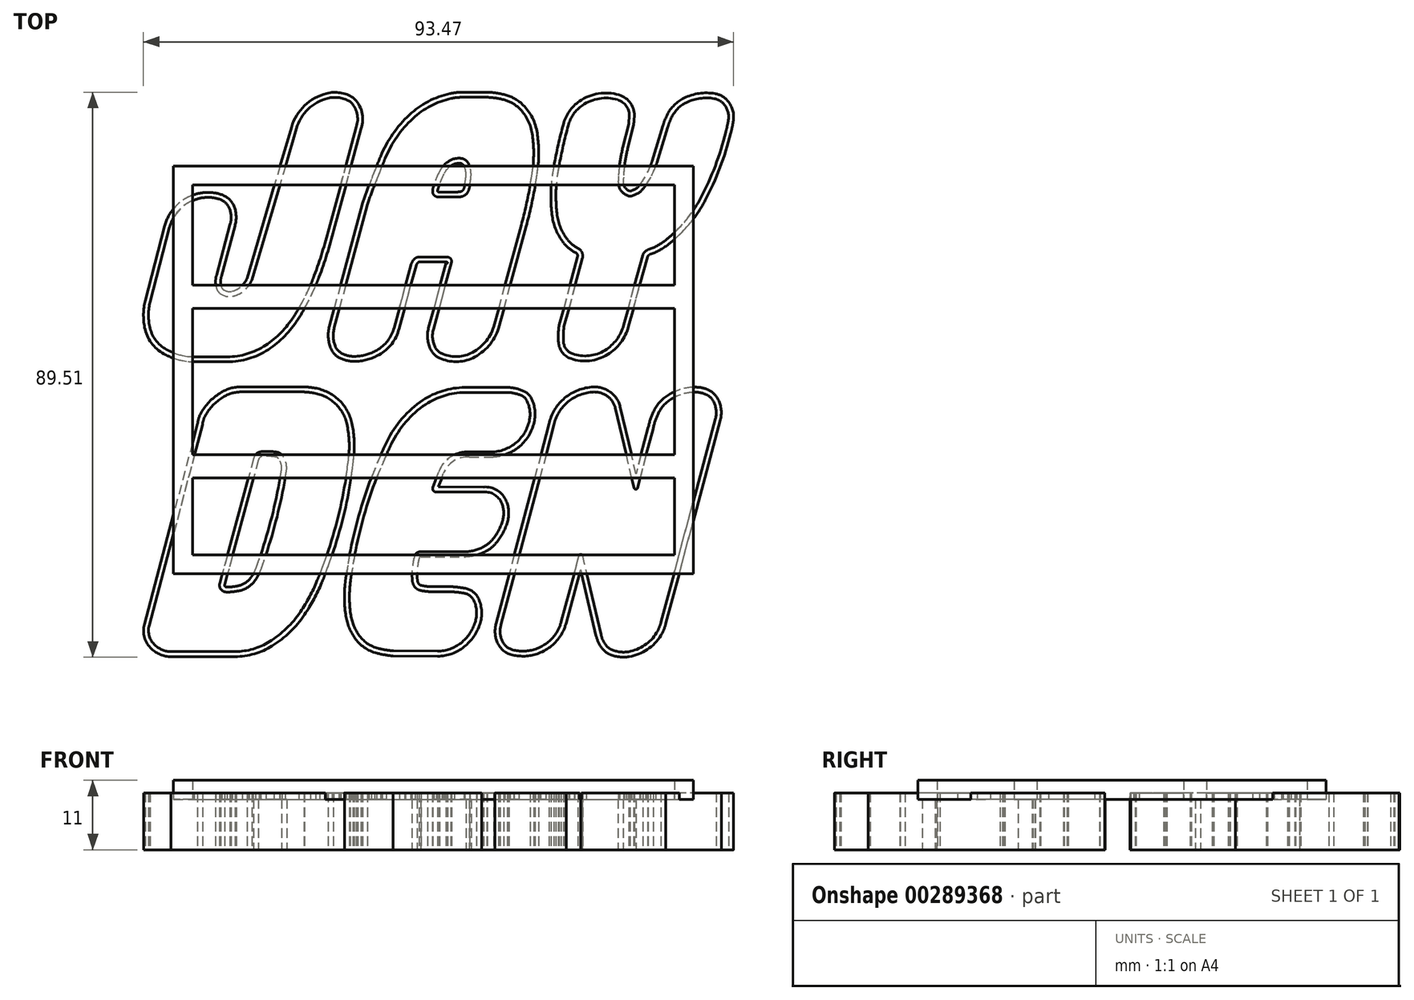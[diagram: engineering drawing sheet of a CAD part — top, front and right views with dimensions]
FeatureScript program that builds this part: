
annotation { "Feature Type Name" : "Feature", "Feature Type Description" : "" }
export const myFeature = defineFeature(function(context is Context, id is Id, definition is map)
    precondition{}
    {
        {
            var Q0;
            Q0=qCreatedBy(makeId("Top.planeOp"),FACE);
            var sketch = newSketch(context, id + "F0", { "sketchPlane" : qUnion([Q0])});
            skLineSegment(sketch, "E0", {"start": v(-12.96, 39.12) * mm, "end": v(-17.26, 23) * mm});
            skArc(sketch, "E1", {"start": v(-17.26, 23) * mm, "mid": v(-18.34, 19.28) * mm, "end": v(-19.6, 15.63) * mm});
            skArc(sketch, "E2", {"start": v(-19.6, 15.63) * mm, "mid": v(-21.14, 12.1) * mm, "end": v(-23.08, 8.76) * mm});
            skArc(sketch, "E3", {"start": v(-23.08, 8.76) * mm, "mid": v(-25.13, 6.3) * mm, "end": v(-27.66, 4.35) * mm});
            skArc(sketch, "E4", {"start": v(-27.66, 4.35) * mm, "mid": v(-30.6, 3.1) * mm, "end": v(-33.77, 2.75) * mm});
            skLineSegment(sketch, "E5", {"start": v(-33.77, 2.75) * mm, "end": v(-38.52, 2.75) * mm});
            skArc(sketch, "E6", {"start": v(-38.52, 2.75) * mm, "mid": v(-40.84, 3.04) * mm, "end": v(-43.02, 3.9) * mm});
            skArc(sketch, "E7", {"start": v(-43.02, 3.9) * mm, "mid": v(-44.75, 5.43) * mm, "end": v(-45.68, 7.55) * mm});
            skArc(sketch, "E8", {"start": v(-45.68, 7.55) * mm, "mid": v(-45.85, 9.5) * mm, "end": v(-45.6, 11.44) * mm});
            skLineSegment(sketch, "E9", {"start": v(-45.6, 11.44) * mm, "end": v(-42.52, 23.25) * mm});
            skArc(sketch, "E10", {"start": v(-42.52, 23.25) * mm, "mid": v(-40.4, 26.55) * mm, "end": v(-36.76, 27.98) * mm});
            skArc(sketch, "E11", {"start": v(-36.76, 27.98) * mm, "mid": v(-35.62, 27.94) * mm, "end": v(-34.51, 27.67) * mm});
            skArc(sketch, "E12", {"start": v(-34.51, 27.67) * mm, "mid": v(-33.6, 27.1) * mm, "end": v(-33.02, 26.22) * mm});
            skArc(sketch, "E13", {"start": v(-33.02, 26.22) * mm, "mid": v(-32.77, 24.97) * mm, "end": v(-32.93, 23.7) * mm});
            skLineSegment(sketch, "E14", {"start": v(-32.93, 23.7) * mm, "end": v(-35.1, 15.7) * mm});
            skArc(sketch, "E15", {"start": v(-35.1, 15.7) * mm, "mid": v(-35.23, 14.66) * mm, "end": v(-35.1, 13.63) * mm});
            skArc(sketch, "E16", {"start": v(-35.1, 13.63) * mm, "mid": v(-34.93, 13.22) * mm, "end": v(-34.64, 12.89) * mm});
            skArc(sketch, "E17", {"start": v(-34.64, 12.89) * mm, "mid": v(-33.6, 12.35) * mm, "end": v(-32.42, 12.35) * mm});
            skArc(sketch, "E18", {"start": v(-32.42, 12.35) * mm, "mid": v(-30.64, 13.29) * mm, "end": v(-29.5, 14.94) * mm});
            skLineSegment(sketch, "E19", {"start": v(-29.5, 14.94) * mm, "end": v(-22.42, 38.92) * mm});
            skArc(sketch, "E20", {"start": v(-22.42, 38.92) * mm, "mid": v(-20.57, 41.97) * mm, "end": v(-17.45, 43.7) * mm});
            skArc(sketch, "E21", {"start": v(-17.45, 43.7) * mm, "mid": v(-15.64, 43.79) * mm, "end": v(-13.94, 43.18) * mm});
            skArc(sketch, "E22", {"start": v(-13.94, 43.18) * mm, "mid": v(-12.83, 41.3) * mm, "end": v(-12.96, 39.12) * mm});
            skLineSegment(sketch, "E23", {"start": v(8.82, 7.5) * mm, "end": v(13.19, 23.62) * mm});
            skArc(sketch, "E24", {"start": v(13.19, 23.62) * mm, "mid": v(14.17, 27.72) * mm, "end": v(14.91, 31.87) * mm});
            skArc(sketch, "E25", {"start": v(14.91, 31.87) * mm, "mid": v(15.15, 34.97) * mm, "end": v(14.92, 38.07) * mm});
            skArc(sketch, "E26", {"start": v(14.92, 38.07) * mm, "mid": v(14.24, 40.23) * mm, "end": v(12.92, 42.06) * mm});
            skArc(sketch, "E27", {"start": v(12.92, 42.06) * mm, "mid": v(11.83, 42.9) * mm, "end": v(10.57, 43.43) * mm});
            skArc(sketch, "E28", {"start": v(10.57, 43.43) * mm, "mid": v(9.18, 43.73) * mm, "end": v(7.76, 43.86) * mm});
            skLineSegment(sketch, "E29", {"start": v(7.76, 43.86) * mm, "end": v(3.8, 43.85) * mm});
            skArc(sketch, "E30", {"start": v(3.8, 43.85) * mm, "mid": v(2.94, 43.8) * mm, "end": v(2.1, 43.67) * mm});
            skArc(sketch, "E31", {"start": v(2.1, 43.67) * mm, "mid": v(-1.17, 42.49) * mm, "end": v(-4, 40.48) * mm});
            skArc(sketch, "E32", {"start": v(-4, 40.48) * mm, "mid": v(-6.51, 37.57) * mm, "end": v(-8.36, 34.2) * mm});
            skArc(sketch, "E33", {"start": v(-8.36, 34.2) * mm, "mid": v(-9.82, 30.55) * mm, "end": v(-11.2, 26.86) * mm});
            skLineSegment(sketch, "E34", {"start": v(-11.2, 26.86) * mm, "end": v(-16.43, 7.36) * mm});
            skArc(sketch, "E35", {"start": v(-16.43, 7.36) * mm, "mid": v(-16.58, 5.89) * mm, "end": v(-16.28, 4.44) * mm});
            skArc(sketch, "E36", {"start": v(-16.28, 4.44) * mm, "mid": v(-15.88, 3.79) * mm, "end": v(-15.28, 3.32) * mm});
            skArc(sketch, "E37", {"start": v(-15.28, 3.32) * mm, "mid": v(-14.19, 2.9) * mm, "end": v(-13.02, 2.81) * mm});
            skArc(sketch, "E38", {"start": v(-13.02, 2.81) * mm, "mid": v(-11.32, 3.1) * mm, "end": v(-9.73, 3.77) * mm});
            skArc(sketch, "E39", {"start": v(-9.73, 3.77) * mm, "mid": v(-7.97, 5.28) * mm, "end": v(-6.94, 7.36) * mm});
            skLineSegment(sketch, "E40", {"start": v(-6.94, 7.36) * mm, "end": v(-4.23, 17.4) * mm});
            skArc(sketch, "E41", {"start": v(-4.23, 17.4) * mm, "mid": v(-4.04, 17.85) * mm, "end": v(-3.74, 18.24) * mm});
            skArc(sketch, "E42", {"start": v(-3.74, 18.24) * mm, "mid": v(-3.4, 18.47) * mm, "end": v(-3.02, 18.56) * mm});
            skLineSegment(sketch, "E43", {"start": v(-3.02, 18.56) * mm, "end": v(1.38, 18.55) * mm});
            skArc(sketch, "E44", {"start": v(1.38, 18.55) * mm, "mid": v(1.6, 18.53) * mm, "end": v(1.8, 18.45) * mm});
            skArc(sketch, "E45", {"start": v(1.8, 18.45) * mm, "mid": v(2.08, 18.17) * mm, "end": v(2.14, 17.79) * mm});
            skLineSegment(sketch, "E46", {"start": v(2.14, 17.79) * mm, "end": v(-0.73, 7.11) * mm});
            skArc(sketch, "E47", {"start": v(-0.73, 7.11) * mm, "mid": v(-0.85, 5.65) * mm, "end": v(-0.45, 4.24) * mm});
            skArc(sketch, "E48", {"start": v(-0.45, 4.24) * mm, "mid": v(-0.03, 3.67) * mm, "end": v(0.56, 3.27) * mm});
            skArc(sketch, "E49", {"start": v(0.56, 3.27) * mm, "mid": v(2.86, 2.77) * mm, "end": v(5.16, 3.29) * mm});
            skArc(sketch, "E50", {"start": v(5.16, 3.29) * mm, "mid": v(7.44, 5) * mm, "end": v(8.82, 7.5) * mm});
            skLineSegment(sketch, "E51", {"start": v(19.96, 7.58) * mm, "end": v(22.88, 18.37) * mm});
            skArc(sketch, "E52", {"start": v(22.88, 18.37) * mm, "mid": v(22.8, 19.28) * mm, "end": v(22.17, 19.95) * mm});
            skArc(sketch, "E53", {"start": v(22.17, 19.95) * mm, "mid": v(21.27, 20.53) * mm, "end": v(20.52, 21.3) * mm});
            skArc(sketch, "E54", {"start": v(20.52, 21.3) * mm, "mid": v(19.44, 23.1) * mm, "end": v(18.88, 25.15) * mm});
            skArc(sketch, "E55", {"start": v(18.88, 25.15) * mm, "mid": v(18.68, 28.94) * mm, "end": v(19.1, 32.72) * mm});
            skArc(sketch, "E56", {"start": v(19.1, 32.72) * mm, "mid": v(19.8, 36.06) * mm, "end": v(20.62, 39.38) * mm});
            skArc(sketch, "E57", {"start": v(20.62, 39.38) * mm, "mid": v(21.45, 41.18) * mm, "end": v(22.86, 42.58) * mm});
            skArc(sketch, "E58", {"start": v(22.86, 42.58) * mm, "mid": v(25.54, 43.65) * mm, "end": v(28.42, 43.47) * mm});
            skArc(sketch, "E59", {"start": v(28.42, 43.47) * mm, "mid": v(29.85, 42.44) * mm, "end": v(30.28, 40.73) * mm});
            skArc(sketch, "E60", {"start": v(30.28, 40.73) * mm, "mid": v(30.24, 40.17) * mm, "end": v(30.2, 39.6) * mm});
            skLineSegment(sketch, "E61", {"start": v(30.2, 39.6) * mm, "end": v(29.28, 35.92) * mm});
            skArc(sketch, "E62", {"start": v(29.28, 35.92) * mm, "mid": v(28.77, 33.27) * mm, "end": v(28.54, 30.58) * mm});
            skArc(sketch, "E63", {"start": v(28.54, 30.58) * mm, "mid": v(28.59, 29.98) * mm, "end": v(28.78, 29.41) * mm});
            skArc(sketch, "E64", {"start": v(28.78, 29.41) * mm, "mid": v(29.4, 28.62) * mm, "end": v(30.32, 28.18) * mm});
            skArc(sketch, "E65", {"start": v(30.32, 28.18) * mm, "mid": v(30.4, 28.18) * mm, "end": v(30.47, 28.18) * mm});
            skArc(sketch, "E66", {"start": v(30.47, 28.18) * mm, "mid": v(31.65, 28.64) * mm, "end": v(32.59, 29.49) * mm});
            skArc(sketch, "E67", {"start": v(32.59, 29.49) * mm, "mid": v(33.8, 31.38) * mm, "end": v(34.65, 33.46) * mm});
            skLineSegment(sketch, "E68", {"start": v(34.65, 33.46) * mm, "end": v(36.38, 39.13) * mm});
            skArc(sketch, "E69", {"start": v(36.38, 39.13) * mm, "mid": v(36.66, 39.93) * mm, "end": v(37, 40.7) * mm});
            skArc(sketch, "E70", {"start": v(37, 40.7) * mm, "mid": v(37.97, 42.05) * mm, "end": v(39.31, 43.01) * mm});
            skArc(sketch, "E71", {"start": v(39.31, 43.01) * mm, "mid": v(41.47, 43.68) * mm, "end": v(43.73, 43.65) * mm});
            skArc(sketch, "E72", {"start": v(43.73, 43.65) * mm, "mid": v(44.6, 43.34) * mm, "end": v(45.3, 42.75) * mm});
            skArc(sketch, "E73", {"start": v(45.3, 42.75) * mm, "mid": v(45.9, 41.58) * mm, "end": v(45.98, 40.26) * mm});
            skArc(sketch, "E74", {"start": v(45.98, 40.26) * mm, "mid": v(45.8, 39.3) * mm, "end": v(45.59, 38.34) * mm});
            skArc(sketch, "E75", {"start": v(45.59, 38.34) * mm, "mid": v(43.9, 32.99) * mm, "end": v(41.6, 27.87) * mm});
            skArc(sketch, "E76", {"start": v(41.6, 27.87) * mm, "mid": v(39.13, 24.22) * mm, "end": v(35.97, 21.16) * mm});
            skArc(sketch, "E77", {"start": v(35.97, 21.16) * mm, "mid": v(34.7, 20.33) * mm, "end": v(33.32, 19.72) * mm});
            skArc(sketch, "E78", {"start": v(33.32, 19.72) * mm, "mid": v(32.78, 19.39) * mm, "end": v(32.43, 18.87) * mm});
            skLineSegment(sketch, "E79", {"start": v(32.43, 18.87) * mm, "end": v(29.4, 7.76) * mm});
            skArc(sketch, "E80", {"start": v(29.4, 7.76) * mm, "mid": v(28.3, 5.48) * mm, "end": v(26.43, 3.77) * mm});
            skArc(sketch, "E81", {"start": v(26.43, 3.77) * mm, "mid": v(23.93, 2.92) * mm, "end": v(21.31, 3.21) * mm});
            skArc(sketch, "E82", {"start": v(21.31, 3.21) * mm, "mid": v(20.32, 3.93) * mm, "end": v(19.88, 5.08) * mm});
            skArc(sketch, "E83", {"start": v(19.88, 5.08) * mm, "mid": v(19.85, 6.33) * mm, "end": v(19.96, 7.58) * mm});
            skLineSegment(sketch, "E84", {"start": v(-37.3, -8.03) * mm, "end": v(-45.74, -39.8) * mm});
            skArc(sketch, "E85", {"start": v(-45.74, -39.8) * mm, "mid": v(-45.72, -41.5) * mm, "end": v(-44.82, -42.95) * mm});
            skArc(sketch, "E86", {"start": v(-44.82, -42.95) * mm, "mid": v(-43.64, -43.7) * mm, "end": v(-42.27, -43.97) * mm});
            skLineSegment(sketch, "E87", {"start": v(-42.27, -43.97) * mm, "end": v(-32.12, -43.95) * mm});
            skArc(sketch, "E88", {"start": v(-32.12, -43.95) * mm, "mid": v(-29.3, -43.55) * mm, "end": v(-26.7, -42.39) * mm});
            skArc(sketch, "E89", {"start": v(-26.7, -42.39) * mm, "mid": v(-24, -40.28) * mm, "end": v(-21.8, -37.65) * mm});
            skArc(sketch, "E90", {"start": v(-21.8, -37.65) * mm, "mid": v(-20.35, -35.26) * mm, "end": v(-19.15, -32.73) * mm});
            skArc(sketch, "E91", {"start": v(-19.15, -32.73) * mm, "mid": v(-16, -23.29) * mm, "end": v(-14.17, -13.5) * mm});
            skArc(sketch, "E92", {"start": v(-14.17, -13.5) * mm, "mid": v(-14.08, -10.68) * mm, "end": v(-14.43, -7.9) * mm});
            skArc(sketch, "E93", {"start": v(-14.43, -7.9) * mm, "mid": v(-15.1, -6.15) * mm, "end": v(-16.24, -4.68) * mm});
            skArc(sketch, "E94", {"start": v(-16.24, -4.68) * mm, "mid": v(-17.84, -3.58) * mm, "end": v(-19.68, -2.98) * mm});
            skArc(sketch, "E95", {"start": v(-19.68, -2.98) * mm, "mid": v(-20.43, -2.88) * mm, "end": v(-21.18, -2.82) * mm});
            skLineSegment(sketch, "E96", {"start": v(-21.18, -2.82) * mm, "end": v(-31.2, -2.82) * mm});
            skArc(sketch, "E97", {"start": v(-31.2, -2.82) * mm, "mid": v(-32.6, -3.01) * mm, "end": v(-33.92, -3.57) * mm});
            skArc(sketch, "E98", {"start": v(-33.92, -3.57) * mm, "mid": v(-35.5, -4.8) * mm, "end": v(-36.73, -6.35) * mm});
            skArc(sketch, "E99", {"start": v(-36.73, -6.35) * mm, "mid": v(-37.1, -7.16) * mm, "end": v(-37.3, -8.03) * mm});
            skLineSegment(sketch, "E100", {"start": v(11, -2.9) * mm, "end": v(4.23, -2.92) * mm});
            skArc(sketch, "E101", {"start": v(4.23, -2.92) * mm, "mid": v(1, -3.4) * mm, "end": v(-1.96, -4.8) * mm});
            skArc(sketch, "E102", {"start": v(-1.96, -4.8) * mm, "mid": v(-5.07, -7.54) * mm, "end": v(-7.35, -11) * mm});
            skArc(sketch, "E103", {"start": v(-7.35, -11) * mm, "mid": v(-11.48, -21.6) * mm, "end": v(-13.86, -32.75) * mm});
            skArc(sketch, "E104", {"start": v(-13.86, -32.75) * mm, "mid": v(-14.03, -35.35) * mm, "end": v(-13.85, -37.95) * mm});
            skArc(sketch, "E105", {"start": v(-13.85, -37.95) * mm, "mid": v(-13.4, -39.7) * mm, "end": v(-12.57, -41.28) * mm});
            skArc(sketch, "E106", {"start": v(-12.57, -41.28) * mm, "mid": v(-11.22, -42.65) * mm, "end": v(-9.47, -43.44) * mm});
            skArc(sketch, "E107", {"start": v(-9.47, -43.44) * mm, "mid": v(-8.28, -43.69) * mm, "end": v(-7.08, -43.84) * mm});
            skLineSegment(sketch, "E108", {"start": v(-7.08, -43.84) * mm, "end": v(-0.05, -43.88) * mm});
            skArc(sketch, "E109", {"start": v(-0.05, -43.88) * mm, "mid": v(1.9, -43.55) * mm, "end": v(3.64, -42.58) * mm});
            skArc(sketch, "E110", {"start": v(3.64, -42.58) * mm, "mid": v(5, -41.12) * mm, "end": v(5.88, -39.33) * mm});
            skArc(sketch, "E111", {"start": v(5.88, -39.33) * mm, "mid": v(6.1, -37.62) * mm, "end": v(5.71, -35.94) * mm});
            skArc(sketch, "E112", {"start": v(5.71, -35.94) * mm, "mid": v(5.1, -35.14) * mm, "end": v(4.19, -34.72) * mm});
            skArc(sketch, "E113", {"start": v(4.19, -34.72) * mm, "mid": v(3.1, -34.56) * mm, "end": v(2, -34.47) * mm});
            skLineSegment(sketch, "E114", {"start": v(2, -34.47) * mm, "end": v(-1, -34.47) * mm});
            skArc(sketch, "E115", {"start": v(-1, -34.47) * mm, "mid": v(-1.94, -34.42) * mm, "end": v(-2.85, -34.25) * mm});
            skArc(sketch, "E116", {"start": v(-2.85, -34.25) * mm, "mid": v(-3.22, -34.11) * mm, "end": v(-3.53, -33.87) * mm});
            skArc(sketch, "E117", {"start": v(-3.53, -33.87) * mm, "mid": v(-3.88, -33.38) * mm, "end": v(-4.05, -32.8) * mm});
            skArc(sketch, "E118", {"start": v(-4.05, -32.8) * mm, "mid": v(-4.08, -30.82) * mm, "end": v(-3.74, -28.88) * mm});
            skArc(sketch, "E119", {"start": v(-3.74, -28.88) * mm, "mid": v(-3.34, -28.32) * mm, "end": v(-2.67, -28.15) * mm});
            skLineSegment(sketch, "E120", {"start": v(-2.67, -28.15) * mm, "end": v(4.14, -28.13) * mm});
            skArc(sketch, "E121", {"start": v(4.14, -28.13) * mm, "mid": v(5.71, -27.94) * mm, "end": v(7.2, -27.37) * mm});
            skArc(sketch, "E122", {"start": v(7.2, -27.37) * mm, "mid": v(7.95, -26.87) * mm, "end": v(8.6, -26.23) * mm});
            skArc(sketch, "E123", {"start": v(8.6, -26.23) * mm, "mid": v(9.56, -24.83) * mm, "end": v(10.22, -23.26) * mm});
            skArc(sketch, "E124", {"start": v(10.22, -23.26) * mm, "mid": v(10.4, -21.83) * mm, "end": v(10.08, -20.43) * mm});
            skArc(sketch, "E125", {"start": v(10.08, -20.43) * mm, "mid": v(8.94, -19.1) * mm, "end": v(7.24, -18.68) * mm});
            skLineSegment(sketch, "E126", {"start": v(7.24, -18.68) * mm, "end": v(-0.3, -18.68) * mm});
            skArc(sketch, "E127", {"start": v(-0.3, -18.68) * mm, "mid": v(-0.75, -18.46) * mm, "end": v(-0.84, -17.97) * mm});
            skLineSegment(sketch, "E128", {"start": v(-0.84, -17.97) * mm, "end": v(0.1, -15.5) * mm});
            skArc(sketch, "E129", {"start": v(0.1, -15.5) * mm, "mid": v(2.02, -13.1) * mm, "end": v(5, -12.34) * mm});
            skLineSegment(sketch, "E130", {"start": v(5, -12.34) * mm, "end": v(8.41, -12.32) * mm});
            skArc(sketch, "E131", {"start": v(8.41, -12.32) * mm, "mid": v(10.55, -11.93) * mm, "end": v(12.43, -10.82) * mm});
            skArc(sketch, "E132", {"start": v(12.43, -10.82) * mm, "mid": v(13.77, -9.18) * mm, "end": v(14.5, -7.2) * mm});
            skArc(sketch, "E133", {"start": v(14.5, -7.2) * mm, "mid": v(14.51, -5.58) * mm, "end": v(14, -4.06) * mm});
            skArc(sketch, "E134", {"start": v(14, -4.06) * mm, "mid": v(13.7, -3.7) * mm, "end": v(13.31, -3.44) * mm});
            skArc(sketch, "E135", {"start": v(13.31, -3.44) * mm, "mid": v(12.18, -3.05) * mm, "end": v(11, -2.9) * mm});
            skLineSegment(sketch, "E136", {"start": v(18.37, -8.07) * mm, "end": v(9.97, -39.71) * mm});
            skArc(sketch, "E137", {"start": v(9.97, -39.71) * mm, "mid": v(9.84, -40.9) * mm, "end": v(10.07, -42.07) * mm});
            skArc(sketch, "E138", {"start": v(10.07, -42.07) * mm, "mid": v(10.76, -43.08) * mm, "end": v(11.83, -43.67) * mm});
            skArc(sketch, "E139", {"start": v(11.83, -43.67) * mm, "mid": v(13.54, -43.88) * mm, "end": v(15.23, -43.63) * mm});
            skArc(sketch, "E140", {"start": v(15.23, -43.63) * mm, "mid": v(17.06, -42.74) * mm, "end": v(18.52, -41.33) * mm});
            skArc(sketch, "E141", {"start": v(18.52, -41.33) * mm, "mid": v(19.12, -40.33) * mm, "end": v(19.52, -39.23) * mm});
            skLineSegment(sketch, "E142", {"start": v(19.52, -39.23) * mm, "end": v(22.34, -28.75) * mm});
            skArc(sketch, "E143", {"start": v(22.34, -28.75) * mm, "mid": v(22.58, -28.55) * mm, "end": v(22.86, -28.7) * mm});
            skLineSegment(sketch, "E144", {"start": v(22.86, -28.7) * mm, "end": v(25.82, -41.3) * mm});
            skArc(sketch, "E145", {"start": v(25.82, -41.3) * mm, "mid": v(26.12, -42.15) * mm, "end": v(26.59, -42.93) * mm});
            skArc(sketch, "E146", {"start": v(26.59, -42.93) * mm, "mid": v(26.97, -43.33) * mm, "end": v(27.44, -43.62) * mm});
            skArc(sketch, "E147", {"start": v(27.44, -43.62) * mm, "mid": v(28.77, -44) * mm, "end": v(30.16, -43.98) * mm});
            skArc(sketch, "E148", {"start": v(30.16, -43.98) * mm, "mid": v(32.71, -42.96) * mm, "end": v(34.62, -40.98) * mm});
            skArc(sketch, "E149", {"start": v(34.62, -40.98) * mm, "mid": v(35.03, -40.18) * mm, "end": v(35.3, -39.33) * mm});
            skLineSegment(sketch, "E150", {"start": v(35.3, -39.33) * mm, "end": v(43.94, -7.08) * mm});
            skArc(sketch, "E151", {"start": v(43.94, -7.08) * mm, "mid": v(44.05, -5.72) * mm, "end": v(43.68, -4.4) * mm});
            skArc(sketch, "E152", {"start": v(43.68, -4.4) * mm, "mid": v(43.14, -3.68) * mm, "end": v(42.39, -3.19) * mm});
            skArc(sketch, "E153", {"start": v(42.39, -3.19) * mm, "mid": v(41.54, -2.93) * mm, "end": v(40.66, -2.86) * mm});
            skArc(sketch, "E154", {"start": v(40.66, -2.86) * mm, "mid": v(38.82, -3.14) * mm, "end": v(37.1, -3.86) * mm});
            skArc(sketch, "E155", {"start": v(37.1, -3.86) * mm, "mid": v(35.84, -4.85) * mm, "end": v(34.91, -6.17) * mm});
            skArc(sketch, "E156", {"start": v(34.91, -6.17) * mm, "mid": v(34.41, -7.38) * mm, "end": v(34.08, -8.65) * mm});
            skLineSegment(sketch, "E157", {"start": v(34.08, -8.65) * mm, "end": v(31.59, -18.04) * mm});
            skArc(sketch, "E158", {"start": v(31.59, -18.04) * mm, "mid": v(31.32, -18.24) * mm, "end": v(31.06, -18.05) * mm});
            skLineSegment(sketch, "E159", {"start": v(31.06, -18.05) * mm, "end": v(28.07, -5.35) * mm});
            skArc(sketch, "E160", {"start": v(28.07, -5.35) * mm, "mid": v(27.61, -4.3) * mm, "end": v(26.8, -3.48) * mm});
            skArc(sketch, "E161", {"start": v(26.8, -3.48) * mm, "mid": v(25.65, -2.95) * mm, "end": v(24.38, -2.84) * mm});
            skArc(sketch, "E162", {"start": v(24.38, -2.84) * mm, "mid": v(22.25, -3.4) * mm, "end": v(20.38, -4.57) * mm});
            skArc(sketch, "E163", {"start": v(20.38, -4.57) * mm, "mid": v(19.08, -6.15) * mm, "end": v(18.37, -8.07) * mm});
            skLineSegment(sketch, "E164", {"start": v(0.26, 28.06) * mm, "end": v(3.14, 28.06) * mm});
            skArc(sketch, "E165", {"start": v(3.14, 28.06) * mm, "mid": v(3.47, 28.08) * mm, "end": v(3.79, 28.14) * mm});
            skArc(sketch, "E166", {"start": v(3.79, 28.14) * mm, "mid": v(4.32, 28.39) * mm, "end": v(4.71, 28.83) * mm});
            skArc(sketch, "E167", {"start": v(4.71, 28.83) * mm, "mid": v(4.88, 29.2) * mm, "end": v(4.99, 29.6) * mm});
            skArc(sketch, "E168", {"start": v(4.99, 29.6) * mm, "mid": v(5.1, 30.3) * mm, "end": v(5.2, 30.99) * mm});
            skArc(sketch, "E169", {"start": v(5.2, 30.99) * mm, "mid": v(5.22, 31.96) * mm, "end": v(5.03, 32.91) * mm});
            skArc(sketch, "E170", {"start": v(5.03, 32.91) * mm, "mid": v(4.7, 33.55) * mm, "end": v(4.15, 34.03) * mm});
            skArc(sketch, "E171", {"start": v(4.15, 34.03) * mm, "mid": v(3.96, 34.12) * mm, "end": v(3.76, 34.17) * mm});
            skArc(sketch, "E172", {"start": v(3.76, 34.17) * mm, "mid": v(2.57, 34.1) * mm, "end": v(1.5, 33.6) * mm});
            skArc(sketch, "E173", {"start": v(1.5, 33.6) * mm, "mid": v(0.75, 32.89) * mm, "end": v(0.19, 32.03) * mm});
            skArc(sketch, "E174", {"start": v(0.19, 32.03) * mm, "mid": v(-0.37, 30.74) * mm, "end": v(-0.8, 29.4) * mm});
            skArc(sketch, "E175", {"start": v(-0.8, 29.4) * mm, "mid": v(-0.86, 29.11) * mm, "end": v(-0.85, 28.81) * mm});
            skArc(sketch, "E176", {"start": v(-0.85, 28.81) * mm, "mid": v(-0.7, 28.42) * mm, "end": v(-0.38, 28.16) * mm});
            skArc(sketch, "E177", {"start": v(-0.38, 28.16) * mm, "mid": v(-0.07, 28.07) * mm, "end": v(0.26, 28.06) * mm});
            skLineSegment(sketch, "E178", {"start": v(-29.21, -13.42) * mm, "end": v(-34.58, -33.17) * mm});
            skArc(sketch, "E179", {"start": v(-34.58, -33.17) * mm, "mid": v(-34.52, -33.88) * mm, "end": v(-34.02, -34.4) * mm});
            skArc(sketch, "E180", {"start": v(-34.02, -34.4) * mm, "mid": v(-33.76, -34.5) * mm, "end": v(-33.48, -34.53) * mm});
            skArc(sketch, "E181", {"start": v(-33.48, -34.53) * mm, "mid": v(-32.44, -34.48) * mm, "end": v(-31.4, -34.3) * mm});
            skArc(sketch, "E182", {"start": v(-31.4, -34.3) * mm, "mid": v(-30.13, -33.78) * mm, "end": v(-29.1, -32.86) * mm});
            skArc(sketch, "E183", {"start": v(-29.1, -32.86) * mm, "mid": v(-28.49, -31.92) * mm, "end": v(-28.02, -30.9) * mm});
            skArc(sketch, "E184", {"start": v(-28.02, -30.9) * mm, "mid": v(-25.66, -23.22) * mm, "end": v(-24.01, -15.37) * mm});
            skArc(sketch, "E185", {"start": v(-24.01, -15.37) * mm, "mid": v(-24.07, -14.05) * mm, "end": v(-24.66, -12.87) * mm});
            skArc(sketch, "E186", {"start": v(-24.66, -12.87) * mm, "mid": v(-25.05, -12.53) * mm, "end": v(-25.53, -12.36) * mm});
            skArc(sketch, "E187", {"start": v(-25.53, -12.36) * mm, "mid": v(-26.76, -12.24) * mm, "end": v(-27.99, -12.28) * mm});
            skArc(sketch, "E188", {"start": v(-27.99, -12.28) * mm, "mid": v(-28.79, -12.65) * mm, "end": v(-29.21, -13.42) * mm});
            skLineSegment(sketch, "E189", {"start": v(-50, -50) * mm, "end": v(50, -50) * mm});
            skLineSegment(sketch, "E190", {"start": v(50, -50) * mm, "end": v(50, 50) * mm});
            skLineSegment(sketch, "E191", {"start": v(50, 50) * mm, "end": v(-50, 50) * mm});
            skLineSegment(sketch, "E192", {"start": v(-50, 50) * mm, "end": v(-50, -50) * mm});
            skSolve(sketch);
        }
        {
            var Q0;
            Q0=qCreatedBy(makeId("Top.planeOp"),FACE);
            var sketch = newSketch(context, id + "F1", { "sketchPlane" : qUnion([Q0])});
            skArc(sketch, "E193.0.0", {"start": v(19.96, 7.58) * mm, "mid": v(19.85, 6.33) * mm, "end": v(19.88, 5.08) * mm});
            skArc(sketch, "E193.0.1", {"start": v(19.88, 5.08) * mm, "mid": v(20.32, 3.93) * mm, "end": v(21.31, 3.21) * mm});
            skArc(sketch, "E193.0.2", {"start": v(21.31, 3.21) * mm, "mid": v(23.93, 2.92) * mm, "end": v(26.43, 3.77) * mm});
            skArc(sketch, "E193.0.3", {"start": v(26.43, 3.77) * mm, "mid": v(28.3, 5.48) * mm, "end": v(29.4, 7.76) * mm});
            skLineSegment(sketch, "E193.0.4", {"start": v(29.4, 7.76) * mm, "end": v(32.43, 18.87) * mm});
            skArc(sketch, "E193.0.5", {"start": v(32.43, 18.87) * mm, "mid": v(32.78, 19.39) * mm, "end": v(33.32, 19.72) * mm});
            skArc(sketch, "E193.0.6", {"start": v(33.32, 19.72) * mm, "mid": v(34.7, 20.33) * mm, "end": v(35.97, 21.16) * mm});
            skArc(sketch, "E193.0.7", {"start": v(35.97, 21.16) * mm, "mid": v(39.13, 24.22) * mm, "end": v(41.6, 27.87) * mm});
            skArc(sketch, "E193.0.8", {"start": v(41.6, 27.87) * mm, "mid": v(43.9, 32.99) * mm, "end": v(45.59, 38.34) * mm});
            skArc(sketch, "E193.0.9", {"start": v(45.59, 38.34) * mm, "mid": v(45.8, 39.3) * mm, "end": v(45.98, 40.26) * mm});
            skArc(sketch, "E193.0.10", {"start": v(45.98, 40.26) * mm, "mid": v(45.9, 41.58) * mm, "end": v(45.3, 42.75) * mm});
            skArc(sketch, "E193.0.11", {"start": v(45.3, 42.75) * mm, "mid": v(44.6, 43.34) * mm, "end": v(43.73, 43.65) * mm});
            skArc(sketch, "E193.0.12", {"start": v(43.73, 43.65) * mm, "mid": v(41.47, 43.68) * mm, "end": v(39.31, 43.01) * mm});
            skArc(sketch, "E193.0.13", {"start": v(39.31, 43.01) * mm, "mid": v(37.97, 42.05) * mm, "end": v(37, 40.7) * mm});
            skArc(sketch, "E193.0.14", {"start": v(37, 40.7) * mm, "mid": v(36.66, 39.93) * mm, "end": v(36.38, 39.13) * mm});
            skLineSegment(sketch, "E193.0.15", {"start": v(36.38, 39.13) * mm, "end": v(34.65, 33.46) * mm});
            skArc(sketch, "E193.0.16", {"start": v(34.65, 33.46) * mm, "mid": v(33.8, 31.38) * mm, "end": v(32.59, 29.49) * mm});
            skArc(sketch, "E193.0.17", {"start": v(32.59, 29.49) * mm, "mid": v(31.65, 28.64) * mm, "end": v(30.47, 28.18) * mm});
            skArc(sketch, "E193.0.18", {"start": v(30.47, 28.18) * mm, "mid": v(30.4, 28.18) * mm, "end": v(30.32, 28.18) * mm});
            skArc(sketch, "E193.0.19", {"start": v(30.32, 28.18) * mm, "mid": v(29.4, 28.62) * mm, "end": v(28.78, 29.41) * mm});
            skArc(sketch, "E193.0.20", {"start": v(28.78, 29.41) * mm, "mid": v(28.59, 29.98) * mm, "end": v(28.54, 30.58) * mm});
            skArc(sketch, "E193.0.21", {"start": v(28.54, 30.58) * mm, "mid": v(28.77, 33.27) * mm, "end": v(29.28, 35.92) * mm});
            skLineSegment(sketch, "E193.0.22", {"start": v(29.28, 35.92) * mm, "end": v(30.2, 39.6) * mm});
            skArc(sketch, "E193.0.23", {"start": v(30.2, 39.6) * mm, "mid": v(30.24, 40.17) * mm, "end": v(30.28, 40.73) * mm});
            skArc(sketch, "E193.0.24", {"start": v(30.28, 40.73) * mm, "mid": v(29.85, 42.44) * mm, "end": v(28.42, 43.47) * mm});
            skArc(sketch, "E193.0.25", {"start": v(28.42, 43.47) * mm, "mid": v(25.54, 43.65) * mm, "end": v(22.86, 42.58) * mm});
            skArc(sketch, "E193.0.26", {"start": v(22.86, 42.58) * mm, "mid": v(21.45, 41.18) * mm, "end": v(20.62, 39.38) * mm});
            skArc(sketch, "E193.0.27", {"start": v(20.62, 39.38) * mm, "mid": v(19.8, 36.06) * mm, "end": v(19.1, 32.72) * mm});
            skArc(sketch, "E193.0.28", {"start": v(19.1, 32.72) * mm, "mid": v(18.68, 28.94) * mm, "end": v(18.88, 25.15) * mm});
            skArc(sketch, "E193.0.29", {"start": v(18.88, 25.15) * mm, "mid": v(19.44, 23.1) * mm, "end": v(20.52, 21.3) * mm});
            skArc(sketch, "E193.0.30", {"start": v(20.52, 21.3) * mm, "mid": v(21.27, 20.53) * mm, "end": v(22.17, 19.95) * mm});
            skArc(sketch, "E193.0.31", {"start": v(22.17, 19.95) * mm, "mid": v(22.8, 19.28) * mm, "end": v(22.88, 18.37) * mm});
            skLineSegment(sketch, "E193.0.32", {"start": v(22.88, 18.37) * mm, "end": v(19.96, 7.58) * mm});
            skArc(sketch, "E193.1.0", {"start": v(0.56, 3.27) * mm, "mid": v(2.86, 2.77) * mm, "end": v(5.16, 3.29) * mm});
            skArc(sketch, "E193.1.1", {"start": v(5.16, 3.29) * mm, "mid": v(7.44, 5) * mm, "end": v(8.82, 7.5) * mm});
            skLineSegment(sketch, "E193.1.2", {"start": v(8.82, 7.5) * mm, "end": v(13.19, 23.62) * mm});
            skArc(sketch, "E193.1.3", {"start": v(13.19, 23.62) * mm, "mid": v(14.17, 27.72) * mm, "end": v(14.91, 31.87) * mm});
            skArc(sketch, "E193.1.4", {"start": v(14.91, 31.87) * mm, "mid": v(15.15, 34.97) * mm, "end": v(14.92, 38.07) * mm});
            skArc(sketch, "E193.1.5", {"start": v(14.92, 38.07) * mm, "mid": v(14.24, 40.23) * mm, "end": v(12.92, 42.06) * mm});
            skArc(sketch, "E193.1.6", {"start": v(12.92, 42.06) * mm, "mid": v(11.83, 42.9) * mm, "end": v(10.57, 43.43) * mm});
            skArc(sketch, "E193.1.7", {"start": v(10.57, 43.43) * mm, "mid": v(9.18, 43.73) * mm, "end": v(7.76, 43.86) * mm});
            skLineSegment(sketch, "E193.1.8", {"start": v(7.76, 43.86) * mm, "end": v(3.8, 43.85) * mm});
            skArc(sketch, "E193.1.9", {"start": v(3.8, 43.85) * mm, "mid": v(2.94, 43.8) * mm, "end": v(2.1, 43.67) * mm});
            skArc(sketch, "E193.1.10", {"start": v(2.1, 43.67) * mm, "mid": v(-1.17, 42.49) * mm, "end": v(-4, 40.48) * mm});
            skArc(sketch, "E193.1.11", {"start": v(-4, 40.48) * mm, "mid": v(-6.51, 37.57) * mm, "end": v(-8.36, 34.2) * mm});
            skArc(sketch, "E193.1.12", {"start": v(-8.36, 34.2) * mm, "mid": v(-9.82, 30.55) * mm, "end": v(-11.2, 26.86) * mm});
            skLineSegment(sketch, "E193.1.13", {"start": v(-11.2, 26.86) * mm, "end": v(-16.43, 7.36) * mm});
            skArc(sketch, "E193.1.14", {"start": v(-16.43, 7.36) * mm, "mid": v(-16.58, 5.89) * mm, "end": v(-16.28, 4.44) * mm});
            skArc(sketch, "E193.1.15", {"start": v(-16.28, 4.44) * mm, "mid": v(-15.88, 3.79) * mm, "end": v(-15.28, 3.32) * mm});
            skArc(sketch, "E193.1.16", {"start": v(-15.28, 3.32) * mm, "mid": v(-14.19, 2.9) * mm, "end": v(-13.02, 2.81) * mm});
            skArc(sketch, "E193.1.17", {"start": v(-13.02, 2.81) * mm, "mid": v(-11.32, 3.1) * mm, "end": v(-9.73, 3.77) * mm});
            skArc(sketch, "E193.1.18", {"start": v(-9.73, 3.77) * mm, "mid": v(-7.97, 5.28) * mm, "end": v(-6.94, 7.36) * mm});
            skLineSegment(sketch, "E193.1.19", {"start": v(-6.94, 7.36) * mm, "end": v(-4.23, 17.4) * mm});
            skArc(sketch, "E193.1.20", {"start": v(-4.23, 17.4) * mm, "mid": v(-4.04, 17.85) * mm, "end": v(-3.74, 18.24) * mm});
            skArc(sketch, "E193.1.21", {"start": v(-3.74, 18.24) * mm, "mid": v(-3.4, 18.47) * mm, "end": v(-3.02, 18.56) * mm});
            skLineSegment(sketch, "E193.1.22", {"start": v(-3.02, 18.56) * mm, "end": v(1.38, 18.55) * mm});
            skArc(sketch, "E193.1.23", {"start": v(1.38, 18.55) * mm, "mid": v(1.6, 18.53) * mm, "end": v(1.8, 18.45) * mm});
            skArc(sketch, "E193.1.24", {"start": v(1.8, 18.45) * mm, "mid": v(2.08, 18.17) * mm, "end": v(2.14, 17.79) * mm});
            skLineSegment(sketch, "E193.1.25", {"start": v(2.14, 17.79) * mm, "end": v(-0.73, 7.11) * mm});
            skArc(sketch, "E193.1.26", {"start": v(-0.73, 7.11) * mm, "mid": v(-0.85, 5.65) * mm, "end": v(-0.45, 4.24) * mm});
            skArc(sketch, "E193.1.27", {"start": v(-0.45, 4.24) * mm, "mid": v(-0.03, 3.67) * mm, "end": v(0.56, 3.27) * mm});
            skArc(sketch, "E193.2.0", {"start": v(-12.96, 39.12) * mm, "mid": v(-12.83, 41.3) * mm, "end": v(-13.94, 43.18) * mm});
            skArc(sketch, "E193.2.1", {"start": v(-13.94, 43.18) * mm, "mid": v(-15.64, 43.79) * mm, "end": v(-17.45, 43.7) * mm});
            skArc(sketch, "E193.2.2", {"start": v(-17.45, 43.7) * mm, "mid": v(-20.57, 41.97) * mm, "end": v(-22.42, 38.92) * mm});
            skLineSegment(sketch, "E193.2.3", {"start": v(-22.42, 38.92) * mm, "end": v(-29.5, 14.94) * mm});
            skArc(sketch, "E193.2.4", {"start": v(-29.5, 14.94) * mm, "mid": v(-30.64, 13.29) * mm, "end": v(-32.42, 12.35) * mm});
            skArc(sketch, "E193.2.5", {"start": v(-32.42, 12.35) * mm, "mid": v(-33.6, 12.35) * mm, "end": v(-34.64, 12.89) * mm});
            skArc(sketch, "E193.2.6", {"start": v(-34.64, 12.89) * mm, "mid": v(-34.93, 13.22) * mm, "end": v(-35.1, 13.63) * mm});
            skArc(sketch, "E193.2.7", {"start": v(-35.1, 13.63) * mm, "mid": v(-35.23, 14.66) * mm, "end": v(-35.1, 15.7) * mm});
            skLineSegment(sketch, "E193.2.8", {"start": v(-35.1, 15.7) * mm, "end": v(-32.93, 23.7) * mm});
            skArc(sketch, "E193.2.9", {"start": v(-32.93, 23.7) * mm, "mid": v(-32.77, 24.97) * mm, "end": v(-33.02, 26.22) * mm});
            skArc(sketch, "E193.2.10", {"start": v(-33.02, 26.22) * mm, "mid": v(-33.6, 27.1) * mm, "end": v(-34.51, 27.67) * mm});
            skArc(sketch, "E193.2.11", {"start": v(-34.51, 27.67) * mm, "mid": v(-35.62, 27.94) * mm, "end": v(-36.76, 27.98) * mm});
            skArc(sketch, "E193.2.12", {"start": v(-36.76, 27.98) * mm, "mid": v(-40.4, 26.55) * mm, "end": v(-42.52, 23.25) * mm});
            skLineSegment(sketch, "E193.2.13", {"start": v(-42.52, 23.25) * mm, "end": v(-45.6, 11.44) * mm});
            skArc(sketch, "E193.2.14", {"start": v(-45.6, 11.44) * mm, "mid": v(-45.85, 9.5) * mm, "end": v(-45.68, 7.55) * mm});
            skArc(sketch, "E193.2.15", {"start": v(-45.68, 7.55) * mm, "mid": v(-44.75, 5.43) * mm, "end": v(-43.02, 3.9) * mm});
            skArc(sketch, "E193.2.16", {"start": v(-43.02, 3.9) * mm, "mid": v(-40.84, 3.04) * mm, "end": v(-38.52, 2.75) * mm});
            skLineSegment(sketch, "E193.2.17", {"start": v(-38.52, 2.75) * mm, "end": v(-33.77, 2.75) * mm});
            skArc(sketch, "E193.2.18", {"start": v(-33.77, 2.75) * mm, "mid": v(-30.6, 3.1) * mm, "end": v(-27.66, 4.35) * mm});
            skArc(sketch, "E193.2.19", {"start": v(-27.66, 4.35) * mm, "mid": v(-25.13, 6.3) * mm, "end": v(-23.08, 8.76) * mm});
            skArc(sketch, "E193.2.20", {"start": v(-23.08, 8.76) * mm, "mid": v(-21.14, 12.1) * mm, "end": v(-19.6, 15.63) * mm});
            skArc(sketch, "E193.2.21", {"start": v(-19.6, 15.63) * mm, "mid": v(-18.34, 19.28) * mm, "end": v(-17.26, 23) * mm});
            skLineSegment(sketch, "E193.2.22", {"start": v(-17.26, 23) * mm, "end": v(-12.96, 39.12) * mm});
            skArc(sketch, "E193.3.0", {"start": v(-33.92, -3.57) * mm, "mid": v(-35.5, -4.8) * mm, "end": v(-36.73, -6.35) * mm});
            skArc(sketch, "E193.3.1", {"start": v(-36.73, -6.35) * mm, "mid": v(-37.1, -7.16) * mm, "end": v(-37.3, -8.03) * mm});
            skLineSegment(sketch, "E193.3.2", {"start": v(-37.3, -8.03) * mm, "end": v(-45.74, -39.8) * mm});
            skArc(sketch, "E193.3.3", {"start": v(-45.74, -39.8) * mm, "mid": v(-45.72, -41.5) * mm, "end": v(-44.82, -42.95) * mm});
            skArc(sketch, "E193.3.4", {"start": v(-44.82, -42.95) * mm, "mid": v(-43.64, -43.7) * mm, "end": v(-42.27, -43.97) * mm});
            skLineSegment(sketch, "E193.3.5", {"start": v(-42.27, -43.97) * mm, "end": v(-32.12, -43.95) * mm});
            skArc(sketch, "E193.3.6", {"start": v(-32.12, -43.95) * mm, "mid": v(-29.3, -43.55) * mm, "end": v(-26.7, -42.39) * mm});
            skArc(sketch, "E193.3.7", {"start": v(-26.7, -42.39) * mm, "mid": v(-24, -40.28) * mm, "end": v(-21.8, -37.65) * mm});
            skArc(sketch, "E193.3.8", {"start": v(-21.8, -37.65) * mm, "mid": v(-20.35, -35.26) * mm, "end": v(-19.15, -32.73) * mm});
            skArc(sketch, "E193.3.9", {"start": v(-19.15, -32.73) * mm, "mid": v(-16, -23.29) * mm, "end": v(-14.17, -13.5) * mm});
            skArc(sketch, "E193.3.10", {"start": v(-14.17, -13.5) * mm, "mid": v(-14.08, -10.68) * mm, "end": v(-14.43, -7.9) * mm});
            skArc(sketch, "E193.3.11", {"start": v(-14.43, -7.9) * mm, "mid": v(-15.1, -6.15) * mm, "end": v(-16.24, -4.68) * mm});
            skArc(sketch, "E193.3.12", {"start": v(-16.24, -4.68) * mm, "mid": v(-17.84, -3.58) * mm, "end": v(-19.68, -2.98) * mm});
            skArc(sketch, "E193.3.13", {"start": v(-19.68, -2.98) * mm, "mid": v(-20.43, -2.88) * mm, "end": v(-21.18, -2.82) * mm});
            skLineSegment(sketch, "E193.3.14", {"start": v(-21.18, -2.82) * mm, "end": v(-31.2, -2.82) * mm});
            skArc(sketch, "E193.3.15", {"start": v(-31.2, -2.82) * mm, "mid": v(-32.6, -3.01) * mm, "end": v(-33.92, -3.57) * mm});
            skArc(sketch, "E193.4.0", {"start": v(14, -4.06) * mm, "mid": v(13.7, -3.7) * mm, "end": v(13.31, -3.44) * mm});
            skArc(sketch, "E193.4.1", {"start": v(13.31, -3.44) * mm, "mid": v(12.18, -3.05) * mm, "end": v(11, -2.9) * mm});
            skLineSegment(sketch, "E193.4.2", {"start": v(11, -2.9) * mm, "end": v(4.23, -2.92) * mm});
            skArc(sketch, "E193.4.3", {"start": v(4.23, -2.92) * mm, "mid": v(1, -3.4) * mm, "end": v(-1.96, -4.8) * mm});
            skArc(sketch, "E193.4.4", {"start": v(-1.96, -4.8) * mm, "mid": v(-5.07, -7.54) * mm, "end": v(-7.35, -11) * mm});
            skArc(sketch, "E193.4.5", {"start": v(-7.35, -11) * mm, "mid": v(-11.48, -21.6) * mm, "end": v(-13.86, -32.75) * mm});
            skArc(sketch, "E193.4.6", {"start": v(-13.86, -32.75) * mm, "mid": v(-14.03, -35.35) * mm, "end": v(-13.85, -37.95) * mm});
            skArc(sketch, "E193.4.7", {"start": v(-13.85, -37.95) * mm, "mid": v(-13.4, -39.7) * mm, "end": v(-12.57, -41.28) * mm});
            skArc(sketch, "E193.4.8", {"start": v(-12.57, -41.28) * mm, "mid": v(-11.22, -42.65) * mm, "end": v(-9.47, -43.44) * mm});
            skArc(sketch, "E193.4.9", {"start": v(-9.47, -43.44) * mm, "mid": v(-8.28, -43.69) * mm, "end": v(-7.08, -43.84) * mm});
            skLineSegment(sketch, "E193.4.10", {"start": v(-7.08, -43.84) * mm, "end": v(-0.05, -43.88) * mm});
            skArc(sketch, "E193.4.11", {"start": v(-0.05, -43.88) * mm, "mid": v(1.9, -43.55) * mm, "end": v(3.64, -42.58) * mm});
            skArc(sketch, "E193.4.12", {"start": v(3.64, -42.58) * mm, "mid": v(5, -41.12) * mm, "end": v(5.88, -39.33) * mm});
            skArc(sketch, "E193.4.13", {"start": v(5.88, -39.33) * mm, "mid": v(6.1, -37.62) * mm, "end": v(5.71, -35.94) * mm});
            skArc(sketch, "E193.4.14", {"start": v(5.71, -35.94) * mm, "mid": v(5.1, -35.14) * mm, "end": v(4.19, -34.72) * mm});
            skArc(sketch, "E193.4.15", {"start": v(4.19, -34.72) * mm, "mid": v(3.1, -34.56) * mm, "end": v(2, -34.47) * mm});
            skLineSegment(sketch, "E193.4.16", {"start": v(2, -34.47) * mm, "end": v(-1, -34.47) * mm});
            skArc(sketch, "E193.4.17", {"start": v(-1, -34.47) * mm, "mid": v(-1.94, -34.42) * mm, "end": v(-2.85, -34.25) * mm});
            skArc(sketch, "E193.4.18", {"start": v(-2.85, -34.25) * mm, "mid": v(-3.22, -34.11) * mm, "end": v(-3.53, -33.87) * mm});
            skArc(sketch, "E193.4.19", {"start": v(-3.53, -33.87) * mm, "mid": v(-3.88, -33.38) * mm, "end": v(-4.05, -32.8) * mm});
            skArc(sketch, "E193.4.20", {"start": v(-4.05, -32.8) * mm, "mid": v(-4.08, -30.82) * mm, "end": v(-3.74, -28.88) * mm});
            skArc(sketch, "E193.4.21", {"start": v(-3.74, -28.88) * mm, "mid": v(-3.34, -28.32) * mm, "end": v(-2.67, -28.15) * mm});
            skLineSegment(sketch, "E193.4.22", {"start": v(-2.67, -28.15) * mm, "end": v(4.14, -28.13) * mm});
            skArc(sketch, "E193.4.23", {"start": v(4.14, -28.13) * mm, "mid": v(5.71, -27.94) * mm, "end": v(7.2, -27.37) * mm});
            skArc(sketch, "E193.4.24", {"start": v(7.2, -27.37) * mm, "mid": v(7.95, -26.87) * mm, "end": v(8.6, -26.23) * mm});
            skArc(sketch, "E193.4.25", {"start": v(8.6, -26.23) * mm, "mid": v(9.56, -24.83) * mm, "end": v(10.22, -23.26) * mm});
            skArc(sketch, "E193.4.26", {"start": v(10.22, -23.26) * mm, "mid": v(10.4, -21.83) * mm, "end": v(10.08, -20.43) * mm});
            skArc(sketch, "E193.4.27", {"start": v(10.08, -20.43) * mm, "mid": v(8.94, -19.1) * mm, "end": v(7.24, -18.68) * mm});
            skLineSegment(sketch, "E193.4.28", {"start": v(7.24, -18.68) * mm, "end": v(-0.3, -18.68) * mm});
            skArc(sketch, "E193.4.29", {"start": v(-0.3, -18.68) * mm, "mid": v(-0.75, -18.46) * mm, "end": v(-0.84, -17.97) * mm});
            skLineSegment(sketch, "E193.4.30", {"start": v(-0.84, -17.97) * mm, "end": v(0.1, -15.5) * mm});
            skArc(sketch, "E193.4.31", {"start": v(0.1, -15.5) * mm, "mid": v(2.02, -13.1) * mm, "end": v(5, -12.34) * mm});
            skLineSegment(sketch, "E193.4.32", {"start": v(5, -12.34) * mm, "end": v(8.41, -12.32) * mm});
            skArc(sketch, "E193.4.33", {"start": v(8.41, -12.32) * mm, "mid": v(10.55, -11.93) * mm, "end": v(12.43, -10.82) * mm});
            skArc(sketch, "E193.4.34", {"start": v(12.43, -10.82) * mm, "mid": v(13.77, -9.18) * mm, "end": v(14.5, -7.2) * mm});
            skArc(sketch, "E193.4.35", {"start": v(14.5, -7.2) * mm, "mid": v(14.51, -5.58) * mm, "end": v(14, -4.06) * mm});
            skArc(sketch, "E193.5.0", {"start": v(24.38, -2.84) * mm, "mid": v(22.25, -3.4) * mm, "end": v(20.38, -4.57) * mm});
            skArc(sketch, "E193.5.1", {"start": v(20.38, -4.57) * mm, "mid": v(19.08, -6.15) * mm, "end": v(18.37, -8.07) * mm});
            skLineSegment(sketch, "E193.5.2", {"start": v(18.37, -8.07) * mm, "end": v(9.97, -39.71) * mm});
            skArc(sketch, "E193.5.3", {"start": v(9.97, -39.71) * mm, "mid": v(9.84, -40.9) * mm, "end": v(10.07, -42.07) * mm});
            skArc(sketch, "E193.5.4", {"start": v(10.07, -42.07) * mm, "mid": v(10.76, -43.08) * mm, "end": v(11.83, -43.67) * mm});
            skArc(sketch, "E193.5.5", {"start": v(11.83, -43.67) * mm, "mid": v(13.54, -43.88) * mm, "end": v(15.23, -43.63) * mm});
            skArc(sketch, "E193.5.6", {"start": v(15.23, -43.63) * mm, "mid": v(17.06, -42.74) * mm, "end": v(18.52, -41.33) * mm});
            skArc(sketch, "E193.5.7", {"start": v(18.52, -41.33) * mm, "mid": v(19.12, -40.33) * mm, "end": v(19.52, -39.23) * mm});
            skLineSegment(sketch, "E193.5.8", {"start": v(19.52, -39.23) * mm, "end": v(22.34, -28.75) * mm});
            skArc(sketch, "E193.5.9", {"start": v(22.34, -28.75) * mm, "mid": v(22.58, -28.55) * mm, "end": v(22.86, -28.7) * mm});
            skLineSegment(sketch, "E193.5.10", {"start": v(22.86, -28.7) * mm, "end": v(25.82, -41.3) * mm});
            skArc(sketch, "E193.5.11", {"start": v(25.82, -41.3) * mm, "mid": v(26.12, -42.15) * mm, "end": v(26.59, -42.93) * mm});
            skArc(sketch, "E193.5.12", {"start": v(26.59, -42.93) * mm, "mid": v(26.97, -43.33) * mm, "end": v(27.44, -43.62) * mm});
            skArc(sketch, "E193.5.13", {"start": v(27.44, -43.62) * mm, "mid": v(28.77, -44) * mm, "end": v(30.16, -43.98) * mm});
            skArc(sketch, "E193.5.14", {"start": v(30.16, -43.98) * mm, "mid": v(32.71, -42.96) * mm, "end": v(34.62, -40.98) * mm});
            skArc(sketch, "E193.5.15", {"start": v(34.62, -40.98) * mm, "mid": v(35.03, -40.18) * mm, "end": v(35.3, -39.33) * mm});
            skLineSegment(sketch, "E193.5.16", {"start": v(35.3, -39.33) * mm, "end": v(43.94, -7.08) * mm});
            skArc(sketch, "E193.5.17", {"start": v(43.94, -7.08) * mm, "mid": v(44.05, -5.72) * mm, "end": v(43.68, -4.4) * mm});
            skArc(sketch, "E193.5.18", {"start": v(43.68, -4.4) * mm, "mid": v(43.14, -3.68) * mm, "end": v(42.39, -3.19) * mm});
            skArc(sketch, "E193.5.19", {"start": v(42.39, -3.19) * mm, "mid": v(41.54, -2.93) * mm, "end": v(40.66, -2.86) * mm});
            skArc(sketch, "E193.5.20", {"start": v(40.66, -2.86) * mm, "mid": v(38.82, -3.14) * mm, "end": v(37.1, -3.86) * mm});
            skArc(sketch, "E193.5.21", {"start": v(37.1, -3.86) * mm, "mid": v(35.84, -4.85) * mm, "end": v(34.91, -6.17) * mm});
            skArc(sketch, "E193.5.22", {"start": v(34.91, -6.17) * mm, "mid": v(34.41, -7.38) * mm, "end": v(34.08, -8.65) * mm});
            skLineSegment(sketch, "E193.5.23", {"start": v(34.08, -8.65) * mm, "end": v(31.59, -18.04) * mm});
            skArc(sketch, "E193.5.24", {"start": v(31.59, -18.04) * mm, "mid": v(31.32, -18.24) * mm, "end": v(31.06, -18.05) * mm});
            skLineSegment(sketch, "E193.5.25", {"start": v(31.06, -18.05) * mm, "end": v(28.07, -5.35) * mm});
            skArc(sketch, "E193.5.26", {"start": v(28.07, -5.35) * mm, "mid": v(27.61, -4.3) * mm, "end": v(26.8, -3.48) * mm});
            skArc(sketch, "E193.5.27", {"start": v(26.8, -3.48) * mm, "mid": v(25.65, -2.95) * mm, "end": v(24.38, -2.84) * mm});
            skArc(sketch, "E194.0.0", {"start": v(-25.53, -12.36) * mm, "mid": v(-26.76, -12.24) * mm, "end": v(-27.99, -12.28) * mm});
            skArc(sketch, "E194.0.1", {"start": v(-27.99, -12.28) * mm, "mid": v(-28.79, -12.65) * mm, "end": v(-29.21, -13.42) * mm});
            skLineSegment(sketch, "E194.0.2", {"start": v(-29.21, -13.42) * mm, "end": v(-34.58, -33.17) * mm});
            skArc(sketch, "E194.0.3", {"start": v(-34.58, -33.17) * mm, "mid": v(-34.52, -33.88) * mm, "end": v(-34.02, -34.4) * mm});
            skArc(sketch, "E194.0.4", {"start": v(-34.02, -34.4) * mm, "mid": v(-33.76, -34.5) * mm, "end": v(-33.48, -34.53) * mm});
            skArc(sketch, "E194.0.5", {"start": v(-33.48, -34.53) * mm, "mid": v(-32.44, -34.48) * mm, "end": v(-31.4, -34.3) * mm});
            skArc(sketch, "E194.0.6", {"start": v(-31.4, -34.3) * mm, "mid": v(-30.13, -33.78) * mm, "end": v(-29.1, -32.86) * mm});
            skArc(sketch, "E194.0.7", {"start": v(-29.1, -32.86) * mm, "mid": v(-28.49, -31.92) * mm, "end": v(-28.02, -30.9) * mm});
            skArc(sketch, "E194.0.8", {"start": v(-28.02, -30.9) * mm, "mid": v(-25.66, -23.22) * mm, "end": v(-24.01, -15.37) * mm});
            skArc(sketch, "E194.0.9", {"start": v(-24.01, -15.37) * mm, "mid": v(-24.07, -14.05) * mm, "end": v(-24.66, -12.87) * mm});
            skArc(sketch, "E194.0.10", {"start": v(-24.66, -12.87) * mm, "mid": v(-25.05, -12.53) * mm, "end": v(-25.53, -12.36) * mm});
            skArc(sketch, "E194.1.0", {"start": v(-0.85, 28.81) * mm, "mid": v(-0.7, 28.42) * mm, "end": v(-0.38, 28.16) * mm});
            skArc(sketch, "E194.1.1", {"start": v(-0.38, 28.16) * mm, "mid": v(-0.07, 28.07) * mm, "end": v(0.26, 28.06) * mm});
            skLineSegment(sketch, "E194.1.2", {"start": v(0.26, 28.06) * mm, "end": v(3.14, 28.06) * mm});
            skArc(sketch, "E194.1.3", {"start": v(3.14, 28.06) * mm, "mid": v(3.47, 28.08) * mm, "end": v(3.79, 28.14) * mm});
            skArc(sketch, "E194.1.4", {"start": v(3.79, 28.14) * mm, "mid": v(4.32, 28.39) * mm, "end": v(4.71, 28.83) * mm});
            skArc(sketch, "E194.1.5", {"start": v(4.71, 28.83) * mm, "mid": v(4.88, 29.2) * mm, "end": v(4.99, 29.6) * mm});
            skArc(sketch, "E194.1.6", {"start": v(4.99, 29.6) * mm, "mid": v(5.1, 30.3) * mm, "end": v(5.2, 30.99) * mm});
            skArc(sketch, "E194.1.7", {"start": v(5.2, 30.99) * mm, "mid": v(5.22, 31.96) * mm, "end": v(5.03, 32.91) * mm});
            skArc(sketch, "E194.1.8", {"start": v(5.03, 32.91) * mm, "mid": v(4.7, 33.55) * mm, "end": v(4.15, 34.03) * mm});
            skArc(sketch, "E194.1.9", {"start": v(4.15, 34.03) * mm, "mid": v(3.96, 34.12) * mm, "end": v(3.76, 34.17) * mm});
            skArc(sketch, "E194.1.10", {"start": v(3.76, 34.17) * mm, "mid": v(2.57, 34.1) * mm, "end": v(1.5, 33.6) * mm});
            skArc(sketch, "E194.1.11", {"start": v(1.5, 33.6) * mm, "mid": v(0.75, 32.89) * mm, "end": v(0.19, 32.03) * mm});
            skArc(sketch, "E194.1.12", {"start": v(0.19, 32.03) * mm, "mid": v(-0.37, 30.74) * mm, "end": v(-0.8, 29.4) * mm});
            skArc(sketch, "E194.1.13", {"start": v(-0.8, 29.4) * mm, "mid": v(-0.86, 29.11) * mm, "end": v(-0.85, 28.81) * mm});
            skSolve(sketch);
        }
        {
            var Q0;
            Q0=makeQuery(id+"F1.imprint","IMPRINT",FACE,{"disambiguationData":[TD([[makeQuery(id+"F1.imprint","IMPRINT",EDGE,{"derivedFrom":sQuery(id+"F1.wireOp",EDGE,"E193.3.0")}),1.0]])]});
            var Q1;
            Q1=makeQuery(id+"F1.imprint","IMPRINT",FACE,{"disambiguationData":[TD([[makeQuery(id+"F1.imprint","IMPRINT",EDGE,{"derivedFrom":sQuery(id+"F1.wireOp",EDGE,"E193.2.0")}),1.0]])]});
            var Q2;
            Q2=makeQuery(id+"F1.imprint","IMPRINT",FACE,{"disambiguationData":[TD([[makeQuery(id+"F1.imprint","IMPRINT",EDGE,{"derivedFrom":sQuery(id+"F1.wireOp",EDGE,"E193.1.0")}),1.0]])]});
            var Q3;
            Q3=makeQuery(id+"F1.imprint","IMPRINT",FACE,{"disambiguationData":[TD([[makeQuery(id+"F1.imprint","IMPRINT",EDGE,{"derivedFrom":sQuery(id+"F1.wireOp",EDGE,"E193.0.0")}),1.0]])]});
            var Q4;
            Q4=makeQuery(id+"F1.imprint","IMPRINT",FACE,{"disambiguationData":[TD([[makeQuery(id+"F1.imprint","IMPRINT",EDGE,{"derivedFrom":sQuery(id+"F1.wireOp",EDGE,"E193.5.0")}),1.0]])]});
            var Q5;
            Q5=makeQuery(id+"F1.imprint","IMPRINT",FACE,{"disambiguationData":[TD([[makeQuery(id+"F1.imprint","IMPRINT",EDGE,{"derivedFrom":sQuery(id+"F1.wireOp",EDGE,"E193.4.0")}),1.0]])]});
            extrude(context, id + "F2", {"entities" : qUnion([Q0, Q1, Q2, Q3, Q4, Q5]), "depth" : 10 * mm});
        }
        {
            var Q0;
            Q0=makeQuery(id+"F2.opExtrude","CAP_FACE",FACE,{"disambiguationData":[OSD([sQuery(id+"F1.wireOp",EDGE,"E193.2.0"),sQuery(id+"F1.wireOp",EDGE,"E193.2.1"),sQuery(id+"F1.wireOp",EDGE,"E193.2.2"),sQuery(id+"F1.wireOp",EDGE,"E193.2.3"),sQuery(id+"F1.wireOp",EDGE,"E193.2.4"),sQuery(id+"F1.wireOp",EDGE,"E193.2.5"),sQuery(id+"F1.wireOp",EDGE,"E193.2.6"),sQuery(id+"F1.wireOp",EDGE,"E193.2.7"),sQuery(id+"F1.wireOp",EDGE,"E193.2.8"),sQuery(id+"F1.wireOp",EDGE,"E193.2.9"),sQuery(id+"F1.wireOp",EDGE,"E193.2.10"),sQuery(id+"F1.wireOp",EDGE,"E193.2.11"),sQuery(id+"F1.wireOp",EDGE,"E193.2.12"),sQuery(id+"F1.wireOp",EDGE,"E193.2.13"),sQuery(id+"F1.wireOp",EDGE,"E193.2.14"),sQuery(id+"F1.wireOp",EDGE,"E193.2.15"),sQuery(id+"F1.wireOp",EDGE,"E193.2.16"),sQuery(id+"F1.wireOp",EDGE,"E193.2.17"),sQuery(id+"F1.wireOp",EDGE,"E193.2.18"),sQuery(id+"F1.wireOp",EDGE,"E193.2.19"),sQuery(id+"F1.wireOp",EDGE,"E193.2.20"),sQuery(id+"F1.wireOp",EDGE,"E193.2.21"),sQuery(id+"F1.wireOp",EDGE,"E193.2.22")])],"isStart":true});
            var Q1;
            Q1=makeQuery(id+"F2.opExtrude","CAP_FACE",FACE,{"disambiguationData":[OSD([sQuery(id+"F1.wireOp",EDGE,"E193.1.0"),sQuery(id+"F1.wireOp",EDGE,"E193.1.1"),sQuery(id+"F1.wireOp",EDGE,"E193.1.2"),sQuery(id+"F1.wireOp",EDGE,"E193.1.3"),sQuery(id+"F1.wireOp",EDGE,"E193.1.4"),sQuery(id+"F1.wireOp",EDGE,"E193.1.5"),sQuery(id+"F1.wireOp",EDGE,"E193.1.6"),sQuery(id+"F1.wireOp",EDGE,"E193.1.7"),sQuery(id+"F1.wireOp",EDGE,"E193.1.8"),sQuery(id+"F1.wireOp",EDGE,"E193.1.9"),sQuery(id+"F1.wireOp",EDGE,"E193.1.10"),sQuery(id+"F1.wireOp",EDGE,"E193.1.11"),sQuery(id+"F1.wireOp",EDGE,"E193.1.12"),sQuery(id+"F1.wireOp",EDGE,"E193.1.13"),sQuery(id+"F1.wireOp",EDGE,"E193.1.14"),sQuery(id+"F1.wireOp",EDGE,"E193.1.15"),sQuery(id+"F1.wireOp",EDGE,"E193.1.16"),sQuery(id+"F1.wireOp",EDGE,"E193.1.17"),sQuery(id+"F1.wireOp",EDGE,"E193.1.18"),sQuery(id+"F1.wireOp",EDGE,"E193.1.19"),sQuery(id+"F1.wireOp",EDGE,"E193.1.20"),sQuery(id+"F1.wireOp",EDGE,"E193.1.21"),sQuery(id+"F1.wireOp",EDGE,"E193.1.22"),sQuery(id+"F1.wireOp",EDGE,"E193.1.23"),sQuery(id+"F1.wireOp",EDGE,"E193.1.24"),sQuery(id+"F1.wireOp",EDGE,"E193.1.25"),sQuery(id+"F1.wireOp",EDGE,"E193.1.26"),sQuery(id+"F1.wireOp",EDGE,"E193.1.27"),sQuery(id+"F1.wireOp",EDGE,"E194.1.0"),sQuery(id+"F1.wireOp",EDGE,"E194.1.1"),sQuery(id+"F1.wireOp",EDGE,"E194.1.2"),sQuery(id+"F1.wireOp",EDGE,"E194.1.3"),sQuery(id+"F1.wireOp",EDGE,"E194.1.4"),sQuery(id+"F1.wireOp",EDGE,"E194.1.5"),sQuery(id+"F1.wireOp",EDGE,"E194.1.6"),sQuery(id+"F1.wireOp",EDGE,"E194.1.7"),sQuery(id+"F1.wireOp",EDGE,"E194.1.8"),sQuery(id+"F1.wireOp",EDGE,"E194.1.9"),sQuery(id+"F1.wireOp",EDGE,"E194.1.10"),sQuery(id+"F1.wireOp",EDGE,"E194.1.11"),sQuery(id+"F1.wireOp",EDGE,"E194.1.12"),sQuery(id+"F1.wireOp",EDGE,"E194.1.13")])],"isStart":true});
            var Q2;
            Q2=makeQuery(id+"F2.opExtrude","CAP_FACE",FACE,{"disambiguationData":[OSD([sQuery(id+"F1.wireOp",EDGE,"E193.0.0"),sQuery(id+"F1.wireOp",EDGE,"E193.0.1"),sQuery(id+"F1.wireOp",EDGE,"E193.0.2"),sQuery(id+"F1.wireOp",EDGE,"E193.0.3"),sQuery(id+"F1.wireOp",EDGE,"E193.0.4"),sQuery(id+"F1.wireOp",EDGE,"E193.0.5"),sQuery(id+"F1.wireOp",EDGE,"E193.0.6"),sQuery(id+"F1.wireOp",EDGE,"E193.0.7"),sQuery(id+"F1.wireOp",EDGE,"E193.0.8"),sQuery(id+"F1.wireOp",EDGE,"E193.0.9"),sQuery(id+"F1.wireOp",EDGE,"E193.0.10"),sQuery(id+"F1.wireOp",EDGE,"E193.0.11"),sQuery(id+"F1.wireOp",EDGE,"E193.0.12"),sQuery(id+"F1.wireOp",EDGE,"E193.0.13"),sQuery(id+"F1.wireOp",EDGE,"E193.0.14"),sQuery(id+"F1.wireOp",EDGE,"E193.0.15"),sQuery(id+"F1.wireOp",EDGE,"E193.0.16"),sQuery(id+"F1.wireOp",EDGE,"E193.0.17"),sQuery(id+"F1.wireOp",EDGE,"E193.0.18"),sQuery(id+"F1.wireOp",EDGE,"E193.0.19"),sQuery(id+"F1.wireOp",EDGE,"E193.0.20"),sQuery(id+"F1.wireOp",EDGE,"E193.0.21"),sQuery(id+"F1.wireOp",EDGE,"E193.0.22"),sQuery(id+"F1.wireOp",EDGE,"E193.0.23"),sQuery(id+"F1.wireOp",EDGE,"E193.0.24"),sQuery(id+"F1.wireOp",EDGE,"E193.0.25"),sQuery(id+"F1.wireOp",EDGE,"E193.0.26"),sQuery(id+"F1.wireOp",EDGE,"E193.0.27"),sQuery(id+"F1.wireOp",EDGE,"E193.0.28"),sQuery(id+"F1.wireOp",EDGE,"E193.0.29"),sQuery(id+"F1.wireOp",EDGE,"E193.0.30"),sQuery(id+"F1.wireOp",EDGE,"E193.0.31"),sQuery(id+"F1.wireOp",EDGE,"E193.0.32")])],"isStart":true});
            var Q3;
            Q3=makeQuery(id+"F2.opExtrude","CAP_FACE",FACE,{"disambiguationData":[OSD([sQuery(id+"F1.wireOp",EDGE,"E193.5.0"),sQuery(id+"F1.wireOp",EDGE,"E193.5.1"),sQuery(id+"F1.wireOp",EDGE,"E193.5.2"),sQuery(id+"F1.wireOp",EDGE,"E193.5.3"),sQuery(id+"F1.wireOp",EDGE,"E193.5.4"),sQuery(id+"F1.wireOp",EDGE,"E193.5.5"),sQuery(id+"F1.wireOp",EDGE,"E193.5.6"),sQuery(id+"F1.wireOp",EDGE,"E193.5.7"),sQuery(id+"F1.wireOp",EDGE,"E193.5.8"),sQuery(id+"F1.wireOp",EDGE,"E193.5.9"),sQuery(id+"F1.wireOp",EDGE,"E193.5.10"),sQuery(id+"F1.wireOp",EDGE,"E193.5.11"),sQuery(id+"F1.wireOp",EDGE,"E193.5.12"),sQuery(id+"F1.wireOp",EDGE,"E193.5.13"),sQuery(id+"F1.wireOp",EDGE,"E193.5.14"),sQuery(id+"F1.wireOp",EDGE,"E193.5.15"),sQuery(id+"F1.wireOp",EDGE,"E193.5.16"),sQuery(id+"F1.wireOp",EDGE,"E193.5.17"),sQuery(id+"F1.wireOp",EDGE,"E193.5.18"),sQuery(id+"F1.wireOp",EDGE,"E193.5.19"),sQuery(id+"F1.wireOp",EDGE,"E193.5.20"),sQuery(id+"F1.wireOp",EDGE,"E193.5.21"),sQuery(id+"F1.wireOp",EDGE,"E193.5.22"),sQuery(id+"F1.wireOp",EDGE,"E193.5.23"),sQuery(id+"F1.wireOp",EDGE,"E193.5.24"),sQuery(id+"F1.wireOp",EDGE,"E193.5.25"),sQuery(id+"F1.wireOp",EDGE,"E193.5.26"),sQuery(id+"F1.wireOp",EDGE,"E193.5.27")])],"isStart":true});
            var Q4;
            Q4=makeQuery(id+"F2.opExtrude","CAP_FACE",FACE,{"disambiguationData":[OSD([sQuery(id+"F1.wireOp",EDGE,"E193.4.0"),sQuery(id+"F1.wireOp",EDGE,"E193.4.1"),sQuery(id+"F1.wireOp",EDGE,"E193.4.2"),sQuery(id+"F1.wireOp",EDGE,"E193.4.3"),sQuery(id+"F1.wireOp",EDGE,"E193.4.4"),sQuery(id+"F1.wireOp",EDGE,"E193.4.5"),sQuery(id+"F1.wireOp",EDGE,"E193.4.6"),sQuery(id+"F1.wireOp",EDGE,"E193.4.7"),sQuery(id+"F1.wireOp",EDGE,"E193.4.8"),sQuery(id+"F1.wireOp",EDGE,"E193.4.9"),sQuery(id+"F1.wireOp",EDGE,"E193.4.10"),sQuery(id+"F1.wireOp",EDGE,"E193.4.11"),sQuery(id+"F1.wireOp",EDGE,"E193.4.12"),sQuery(id+"F1.wireOp",EDGE,"E193.4.13"),sQuery(id+"F1.wireOp",EDGE,"E193.4.14"),sQuery(id+"F1.wireOp",EDGE,"E193.4.15"),sQuery(id+"F1.wireOp",EDGE,"E193.4.16"),sQuery(id+"F1.wireOp",EDGE,"E193.4.17"),sQuery(id+"F1.wireOp",EDGE,"E193.4.18"),sQuery(id+"F1.wireOp",EDGE,"E193.4.19"),sQuery(id+"F1.wireOp",EDGE,"E193.4.20"),sQuery(id+"F1.wireOp",EDGE,"E193.4.21"),sQuery(id+"F1.wireOp",EDGE,"E193.4.22"),sQuery(id+"F1.wireOp",EDGE,"E193.4.23"),sQuery(id+"F1.wireOp",EDGE,"E193.4.24"),sQuery(id+"F1.wireOp",EDGE,"E193.4.25"),sQuery(id+"F1.wireOp",EDGE,"E193.4.26"),sQuery(id+"F1.wireOp",EDGE,"E193.4.27"),sQuery(id+"F1.wireOp",EDGE,"E193.4.28"),sQuery(id+"F1.wireOp",EDGE,"E193.4.29"),sQuery(id+"F1.wireOp",EDGE,"E193.4.30"),sQuery(id+"F1.wireOp",EDGE,"E193.4.31"),sQuery(id+"F1.wireOp",EDGE,"E193.4.32"),sQuery(id+"F1.wireOp",EDGE,"E193.4.33"),sQuery(id+"F1.wireOp",EDGE,"E193.4.34"),sQuery(id+"F1.wireOp",EDGE,"E193.4.35")])],"isStart":true});
            var Q5;
            Q5=makeQuery(id+"F2.opExtrude","CAP_FACE",FACE,{"disambiguationData":[OSD([sQuery(id+"F1.wireOp",EDGE,"E193.3.0"),sQuery(id+"F1.wireOp",EDGE,"E193.3.1"),sQuery(id+"F1.wireOp",EDGE,"E193.3.2"),sQuery(id+"F1.wireOp",EDGE,"E193.3.3"),sQuery(id+"F1.wireOp",EDGE,"E193.3.4"),sQuery(id+"F1.wireOp",EDGE,"E193.3.5"),sQuery(id+"F1.wireOp",EDGE,"E193.3.6"),sQuery(id+"F1.wireOp",EDGE,"E193.3.7"),sQuery(id+"F1.wireOp",EDGE,"E193.3.8"),sQuery(id+"F1.wireOp",EDGE,"E193.3.9"),sQuery(id+"F1.wireOp",EDGE,"E193.3.10"),sQuery(id+"F1.wireOp",EDGE,"E193.3.11"),sQuery(id+"F1.wireOp",EDGE,"E193.3.12"),sQuery(id+"F1.wireOp",EDGE,"E193.3.13"),sQuery(id+"F1.wireOp",EDGE,"E193.3.14"),sQuery(id+"F1.wireOp",EDGE,"E193.3.15"),sQuery(id+"F1.wireOp",EDGE,"E194.0.0"),sQuery(id+"F1.wireOp",EDGE,"E194.0.1"),sQuery(id+"F1.wireOp",EDGE,"E194.0.2"),sQuery(id+"F1.wireOp",EDGE,"E194.0.3"),sQuery(id+"F1.wireOp",EDGE,"E194.0.4"),sQuery(id+"F1.wireOp",EDGE,"E194.0.5"),sQuery(id+"F1.wireOp",EDGE,"E194.0.6"),sQuery(id+"F1.wireOp",EDGE,"E194.0.7"),sQuery(id+"F1.wireOp",EDGE,"E194.0.8"),sQuery(id+"F1.wireOp",EDGE,"E194.0.9"),sQuery(id+"F1.wireOp",EDGE,"E194.0.10")])],"isStart":true});
            shell(context, id + "F3", {"entities" : qUnion([Q0, Q1, Q2, Q3, Q4, Q5]), "thickness" : .8 * mm, "oppositeDirection" : true});
        }
        {
            var Q0;
            Q0=qCreatedBy(makeId("Front.planeOp"),FACE);
            var sketch = newSketch(context, id + "F4", { "sketchPlane" : qUnion([Q0])});
            skLineSegment(sketch, "E195", {"start": v(61.33, 9) * mm, "end": v(-59.74, 9) * mm});
            skLineSegment(sketch, "E196", {"start": v(-59.74, 9) * mm, "end": v(-59.74, 18.67) * mm});
            skLineSegment(sketch, "E197", {"start": v(-59.74, 18.67) * mm, "end": v(61.33, 18.67) * mm});
            skLineSegment(sketch, "E198", {"start": v(61.33, 18.67) * mm, "end": v(61.33, 9) * mm});
            skSolve(sketch);
        }
        {
            var Q0;
            Q0 = qSketchRegion(id + "F4", true);
            extrude(context, id + "F5", {"entities" : qUnion([Q0]), "operationType" : NewBodyOperationType.REMOVE, "endBound" : BoundingType.SYMMETRIC, "oppositeDirection" : true, "depth" : 100 * mm});
        }
        {
            var Q0;
            {var subQ15=sQuery(id+"F1.wireOp",EDGE,"E193.2.0");Q0=makeQuery(id+"F5.boolean.opBoolean","COPY",FACE,{"disambiguationData":[TD([makeQuery(id+"F2.opExtrude","SWEPT_FACE",FACE,{"disambiguationData":[OSD([subQ15])]})])],"derivedFrom":makeQuery(id+"F5.opExtrude","SWEPT_FACE",FACE,{"disambiguationData":[OSD([sQuery(id+"F4.wireOp",EDGE,"E195")])]})});}
            var sketch = newSketch(context, id + "F6", { "sketchPlane" : qUnion([Q0])});
            skLineSegment(sketch, "E199.bottom", {"start": v(-41.9, 32.99) * mm, "end": v(40.43, 32.99) * mm});
            skLineSegment(sketch, "E199.top", {"start": v(-41.9, -31.65) * mm, "end": v(40.43, -31.65) * mm});
            skLineSegment(sketch, "E199.left", {"start": v(-41.9, 32.99) * mm, "end": v(-41.9, -31.65) * mm});
            skLineSegment(sketch, "E199.right", {"start": v(40.43, 32.99) * mm, "end": v(40.43, -31.65) * mm});
            skLineSegment(sketch, "E200.0", {"start": v(-38.9, 29.99) * mm, "end": v(37.43, 29.99) * mm});
            skLineSegment(sketch, "E200.1", {"start": v(-38.9, 29.99) * mm, "end": v(-38.9, 14.08) * mm});
            skLineSegment(sketch, "E200.2", {"start": v(-38.9, -28.65) * mm, "end": v(37.43, -28.65) * mm});
            skLineSegment(sketch, "E201.bottom", {"start": v(-38.9, 10.43) * mm, "end": v(37.43, 10.43) * mm});
            skLineSegment(sketch, "E201.top", {"start": v(-38.9, 14.08) * mm, "end": v(37.43, 14.08) * mm});
            skLineSegment(sketch, "E202.bottom", {"start": v(-38.9, -12.78) * mm, "end": v(37.43, -12.78) * mm});
            skLineSegment(sketch, "E202.top", {"start": v(-38.9, -16.43) * mm, "end": v(37.43, -16.43) * mm});
            skLineSegment(sketch, "E203.trimOffspring", {"start": v(-38.9, 10.43) * mm, "end": v(-38.9, -12.78) * mm});
            skLineSegment(sketch, "E204.trimOffspring", {"start": v(-38.9, -16.43) * mm, "end": v(-38.9, -28.65) * mm});
            skLineSegment(sketch, "E205.trimOffspring", {"start": v(37.43, -16.43) * mm, "end": v(37.43, -28.65) * mm});
            skLineSegment(sketch, "E206.trimOffspring", {"start": v(37.43, 10.43) * mm, "end": v(37.43, -12.78) * mm});
            skLineSegment(sketch, "E207", {"start": v(37.43, 29.99) * mm, "end": v(37.43, 14.08) * mm});
            skSolve(sketch);
        }
        {
            var Q0;
            Q0 = qSketchRegion(id + "F6", true);
            var Q1;
            {var subQ0=sQuery(id+"F6.wireOp",EDGE,"E201.right");Q1=makeQuery(id+"F6.imprint","IMPRINT",FACE,{"disambiguationData":[TD([[makeQuery(id+"F6.imprint","IMPRINT",EDGE,{"derivedFrom":subQ0}),1.0]])]});}
            var Q2;
            {var subQ0=sQuery(id+"F6.wireOp",EDGE,"E201.left");var subQ1=sQuery(id+"F6.wireOp",EDGE,"E201.bottom");var subQ2=makeQuery(id+"F6.imprint","INTERSECT",VERTEX,{"derivedFrom":[sQuery(id+"F6.wireOp",EDGE,"E200.1"),subQ1,subQ0]});Q2=makeQuery(id+"F6.imprint","IMPRINT",FACE,{"disambiguationData":[TD([[makeQuery(id+"F6.imprint","IMPRINT",EDGE,{"disambiguationData":[TD([[subQ2,-1.0]])],"derivedFrom":subQ1}),1.0]])]});}
            var Q3;
            {var subQ0=sQuery(id+"F6.wireOp",EDGE,"E201.bottom");var subQ1=makeQuery(id+"F5.opExtrude","SWEPT_FACE",FACE,{"disambiguationData":[OSD([sQuery(id+"F4.wireOp",EDGE,"E195")])]});var subQ2=sQuery(id+"F1.wireOp",EDGE,"E193.2.20");var subQ3=makeQuery(id+"F5.boolean.opBoolean","INTERSECT",EDGE,{"derivedFrom":[makeQuery(id+"F3.opShell","OFFSET_FACE",FACE,{"disambiguationData":[OSD([subQ2])]}),subQ1]});var subQ4=makeQuery(id+"F6.imprint","INTERSECT",VERTEX,{"derivedFrom":[subQ3,subQ0]});Q3=makeQuery(id+"F6.imprint","IMPRINT",FACE,{"disambiguationData":[TD([[makeQuery(id+"F6.imprint","IMPRINT",EDGE,{"disambiguationData":[TD([[subQ4,-1.0]])],"derivedFrom":subQ0}),1.0]])]});}
            var Q4;
            Q4=makeQuery(id+"F6.imprint","IMPRINT",FACE,{"disambiguationData":[TD([[makeQuery(id+"F6.imprint","IMPRINT",EDGE,{"derivedFrom":sQuery(id+"F6.wireOp",EDGE,"E202.bottom")}),-1.0]])]});
            var Q5;
            {var subQ0=makeQuery(id+"F5.opExtrude","SWEPT_FACE",FACE,{"disambiguationData":[OSD([sQuery(id+"F4.wireOp",EDGE,"E195")])]});var subQ1=sQuery(id+"F1.wireOp",EDGE,"E193.2.5");var subQ2=makeQuery(id+"F5.boolean.opBoolean","INTERSECT",EDGE,{"derivedFrom":[makeQuery(id+"F2.opExtrude","SWEPT_FACE",FACE,{"disambiguationData":[OSD([subQ1])]}),subQ0]});Q5=makeQuery(id+"F6.imprint","IMPRINT",FACE,{"disambiguationData":[TD([[makeQuery(id+"F6.imprint","IMPRINT",EDGE,{"derivedFrom":subQ2}),1.0]])]});}
            var Q6;
            {var subQ0=makeQuery(id+"F5.opExtrude","SWEPT_FACE",FACE,{"disambiguationData":[OSD([sQuery(id+"F4.wireOp",EDGE,"E195")])]});var subQ1=makeQuery(id+"F5.boolean.opBoolean","INTERSECT",EDGE,{"derivedFrom":[makeQuery(id+"F2.opExtrude","SWEPT_FACE",FACE,{"disambiguationData":[OSD([sQuery(id+"F1.wireOp",EDGE,"E193.2.5")])]}),subQ0]});Q6=makeQuery(id+"F6.imprint","IMPRINT",FACE,{"disambiguationData":[TD([[makeQuery(id+"F6.imprint","IMPRINT",EDGE,{"derivedFrom":subQ1}),-1.0]])]});}
            extrude(context, id + "F7", {"entities" : qUnion([Q0, Q1, Q2, Q3, Q4, Q5, Q6]), "operationType" : NewBodyOperationType.ADD, "depth" : 2 * mm, "hasSecondDirection" : true, "secondDirectionOppositeDirection" : true, "secondDirectionDepth" : 1 * mm});
        }
    });
